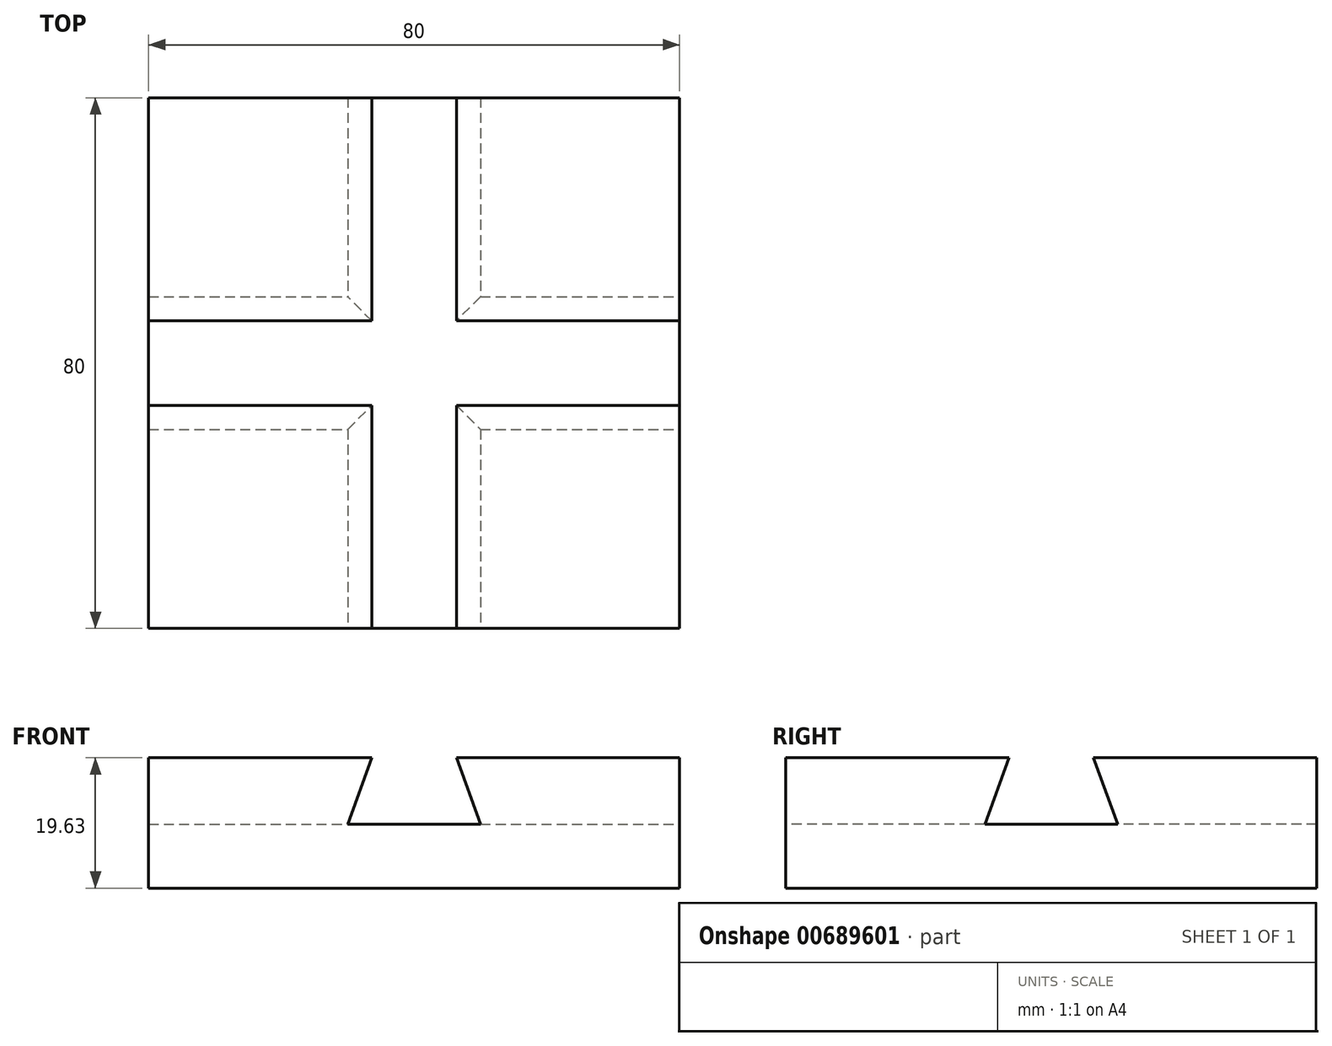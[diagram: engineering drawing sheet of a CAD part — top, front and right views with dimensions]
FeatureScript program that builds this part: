
annotation { "Feature Type Name" : "Feature", "Feature Type Description" : "" }
export const myFeature = defineFeature(function(context is Context, id is Id, definition is map)
    precondition{}
    {
        {
            var Q0;
            Q0=qCreatedBy(makeId("Front.planeOp"),FACE);
            var sketch = newSketch(context, id + "F0", { "sketchPlane" : qUnion([Q0])});
            skLineSegment(sketch, "E0", {"start": v(0, 0) * mm, "end": v(-20, 0) * mm});
            skLineSegment(sketch, "E1", {"start": v(-20, 10) * mm, "end": v(-16.36, 10) * mm});
            skLineSegment(sketch, "E2", {"start": v(0, 10) * mm, "end": v(-3.64, 10) * mm});
            skLineSegment(sketch, "E3", {"start": v(-16.36, 10) * mm, "end": v(-20, 0) * mm});
            skLineSegment(sketch, "E4", {"start": v(0, 0) * mm, "end": v(-3.64, 10) * mm});
            skLineSegment(sketch, "E5", {"start": v(-10, -9.63) * mm, "end": v(30, -9.63) * mm});
            skLineSegment(sketch, "E6", {"start": v(-10, -9.63) * mm, "end": v(-50, -9.63) * mm});
            skLineSegment(sketch, "E7", {"start": v(-50, -9.63) * mm, "end": v(-50, 10) * mm});
            skLineSegment(sketch, "E8", {"start": v(-50, 10) * mm, "end": v(-20, 10) * mm});
            skLineSegment(sketch, "E9", {"start": v(30, -9.63) * mm, "end": v(30, 10) * mm});
            skLineSegment(sketch, "E10", {"start": v(30, 10) * mm, "end": v(-3.64, 10) * mm});
            skLineSegment(sketch, "E11.trimOffspring", {"start": v(-3.64, 10) * mm, "end": v(0, 10) * mm});
            skPoint(sketch, "E12.orphan", {"position": v(-10, 10) * mm});
            skSolve(sketch);
        }
        {
            var Q0;
            Q0=makeQuery(id+"F0.imprint","IMPRINT",FACE,{"disambiguationData":[TD([[makeQuery(id+"F0.imprint","IMPRINT",EDGE,{"derivedFrom":sQuery(id+"F0.wireOp",EDGE,"E0")}),1.0]])]});
            extrude(context, id + "F1", {"entities" : qUnion([Q0]), "oppositeDirection" : true, "depth" : 80 * mm, "offsetDistance" : 25 * mm});
        }
        {
            var Q0;
            Q0=makeQuery(id+"F1.opExtrude","SWEPT_FACE",FACE,{"disambiguationData":[OSD([sQuery(id+"F0.wireOp",EDGE,"E9")])]});
            var sketch = newSketch(context, id + "F2", { "sketchPlane" : qUnion([Q0])});
            skLineSegment(sketch, "E13.bottom", {"start": v(30, 0) * mm, "end": v(50, 0) * mm});
            skLineSegment(sketch, "E13.top", {"start": v(30, 20) * mm, "end": v(50, 20) * mm});
            skPoint(sketch, "E13.middle", {"position": v(40, 10) * mm});
            skLineSegment(sketch, "E14", {"start": v(33.64, 10) * mm, "end": v(30, 0) * mm});
            skLineSegment(sketch, "E15", {"start": v(50, 0) * mm, "end": v(46.36, 10) * mm});
            skSolve(sketch);
        }
        {
            var Q0;
            Q0=makeQuery(id+"F2.imprint","IMPRINT",FACE,{"disambiguationData":[TD([[makeQuery(id+"F2.imprint","IMPRINT",EDGE,{"derivedFrom":sQuery(id+"F2.wireOp",EDGE,"E13.bottom")}),1.0]])]});
            extrude(context, id + "F3", {"entities" : qUnion([Q0]), "operationType" : NewBodyOperationType.REMOVE, "oppositeDirection" : true, "depth" : 80 * mm, "offsetDistance" : 25 * mm});
        }
    });
